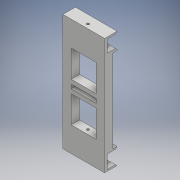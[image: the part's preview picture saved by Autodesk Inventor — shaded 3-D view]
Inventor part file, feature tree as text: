
AUTODESK INVENTOR PART (.ipt)
format: ipt  version: 2018 (Build 220112000, 112)  size: 417,792 bytes
history: native  units: mm
features: extrude x7, sketch x7, chamfer x3
ambient origin geometry x8: Origin, YZ Plane, XZ Plane, XY Plane, X Axis, Y Axis, Z Axis, Center Point
bodies: Solid1 (feature_tree)
feature tree (17):
  extrude  "Extrusion1"  Depth=140.0mm
  extrude  "Extrusion2"  Depth=10.0mm
  extrude  "Extrusion3"  Depth=5.0mm TaperAngle=0.0deg
  extrude  "Extrusion4"  Depth=10.0mm
  extrude  "Extrusion5"  Depth=10.0mm
  chamfer  "Chamfer1"  Distance=5.0mm
  chamfer  "Chamfer2"  Distance=50.0mm
  chamfer  "Chamfer3"  Distance=10.0mm
  extrude  "Extrusion8"  Depth=10.0mm
  extrude  "Extrusion9"  Depth=10.0mm
  sketch  "Sketch1"  dims[d0=50.0mm d1=140.0mm]
  sketch  "Sketch2"  dims[d2=10.0mm d3=0.0mm d4=20.0mm]
  sketch  "Sketch3"  dims[d5=20.0mm d6=5.0mm d7=0.0mm]
  sketch  "Sketch4"  dims[d8=5.0mm d9=10.0mm]
  sketch  "Sketch5"  dims[d10=5.0mm d11=10.0mm d12=5.0mm d13=0.0mm d15=50.0mm d16=0.0mm]
  sketch  "Sketch8"  dims[d17=10.0mm]
  sketch  "Sketch9"  dims[d18=10.0mm d19=10.0mm d21=10.0mm d22=2.5mm d23=5.0mm d24=5.0mm d25=5.0mm d26=10.0mm d27=0.0mm d28=7.0mm d29=2.0mm d30=45.0deg d31=5.0mm d32=2.0mm d33=45.0deg d34=3.0mm d35=2.0mm d36=45.0deg d46=2.0mm d53=5.0mm d54=3.0mm d55=30.0mm d56=0.0mm d57=5.0mm d58=30.0mm d59=0.0mm d60=2.0mm]
